# Revit family: 0053757 Sylvania Lighting Fixture START eco Spikelight IP67 360lm 840 MB BLK
name_source: partatom
category: Lighting Fixtures
revit_build: Autodesk Revit 2016 (Build: 20150220_1215(x64)
units: mm (PartAtom-declared; Revit-internal decimal feet)

## family parameters
Cut with Voids When Loaded = No
Host = Face
Light Source = No
OmniClass Number = 23.80.70.00
OmniClass Title = Lighting
Part Type = Normal
Room Calculation Point = No
Round Connector Dimension = Use Diameter
Shared = No

## types (1)
- 0053757 START eco Spikelight IP67 300lm 840 MB BLK
    Apparent Load = 5 VA
    Assembly Code = D5020200
    AssetType = Fixed
    BracketThickness_SYL = 1 mm  [stored 0.00328084 ft]
    ClassificationName = Uniclass2015
    ClassificationValue = EF_70_80
    Cost = 0 $
    Default Elevation = 1219 mm
    Description = 0
    DocumentationLiterature = http://www.sylvania-lighting.com
    DurationUnit = hours
    ExpectedLife = 50000
    IfcExportAs = IfcLightFixtureType
    IfcExportType = IfcLightFixtureType
    ImpactProtectionIndex = IK08
    IngressProtection = IP67
    InputNominalFrequency = 50/60 Hz
    InputVoltage = 220-240V~
    Keynote = 16500
    Lamp = LED
    LampColourTemperature = 4000 K
    LampNominalLuminous = 300 lm
    LampsType = LED
    LightOutputRatio = 100
    LuminousEfficacy = 83.186 lm/W
    Manufacturer = Feilo Sylvania
    ManufacturerName = Feilo Sylvania
    Material_1_FEILO = Steel, Paint Finish, Dark Gray, Matte
    Material_2_FEILO = <By Category>
    Material_3_FEILO = <By Category>
    Material_4_FEILO = <By Category>
    Model = START eco Spikelight IP67 360lm 840 MB BLK
    ModelNumber = 0053757
    ModelReference = START eco Spikelight IP67 360lm 840 MB BLK
    Name = START eco Spikelight IP67 360lm 840 MB BLK
    NominalDepth = 82 mm  [stored 0.269029 ft]
    NominalHeight = 310 mm
    NominalLength = 70 mm
    PowerConsumption = 4.7 W
    PowerFactor = 0
    SpikeOffset_SYL = 22 mm  [stored 0.0721785 ft]
    SpikeVisibility_SYL = Yes
    Type Image = <None>
    TypeHead_SYL = START eco Spikelight Head : 0053757 START eco Spikelight IP67 300lm 840 MB BLK
    TypeName = 0053757 START eco Spikelight IP67 300lm 840 MB BLK
    URL = http://www.sylvania-lighting.com
    Voltage = 230 V

note: [stored X ft] marks values corroborated as IEEE doubles in the binary element streams (Revit-internal decimal feet)

## geometry (parser evidence)
native form markers: Sweep x5
no freeform markers — native parametric forms only
